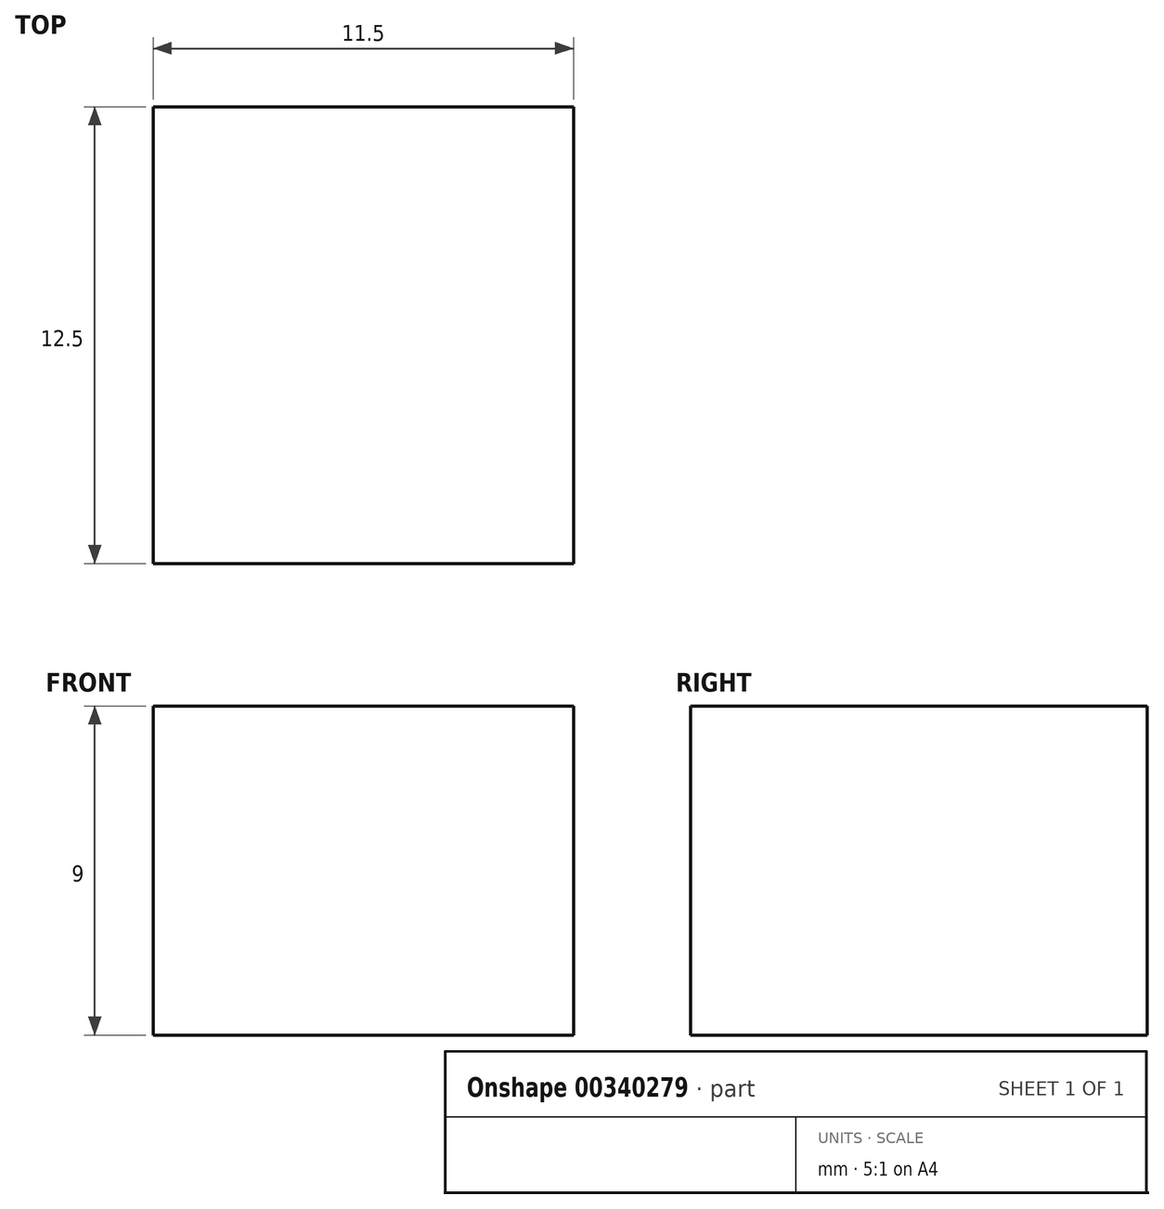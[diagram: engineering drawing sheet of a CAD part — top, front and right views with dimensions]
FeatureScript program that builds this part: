
annotation { "Feature Type Name" : "Feature", "Feature Type Description" : "" }
export const myFeature = defineFeature(function(context is Context, id is Id, definition is map)
    precondition{}
    {
        {
            var Q0;
            Q0=qCreatedBy(makeId("Front.planeOp"),FACE);
            var sketch = newSketch(context, id + "F0", { "sketchPlane" : qUnion([Q0])});
            skLineSegment(sketch, "E0.bottom", {"start": v(-5.75, 4.5) * mm, "end": v(5.75, 4.5) * mm});
            skLineSegment(sketch, "E0.top", {"start": v(-5.75, -4.5) * mm, "end": v(5.75, -4.5) * mm});
            skLineSegment(sketch, "E0.left", {"start": v(-5.75, 4.5) * mm, "end": v(-5.75, -4.5) * mm});
            skLineSegment(sketch, "E0.right", {"start": v(5.75, 4.5) * mm, "end": v(5.75, -4.5) * mm});
            skPoint(sketch, "E0.middle", {"position": v(0, 0) * mm});
            skSolve(sketch);
        }
        {
            var Q0;
            Q0 = qSketchRegion(id + "F0", true);
            extrude(context, id + "F1", {"entities" : qUnion([Q0]), "depth" : 12.5 * mm});
        }
    });
